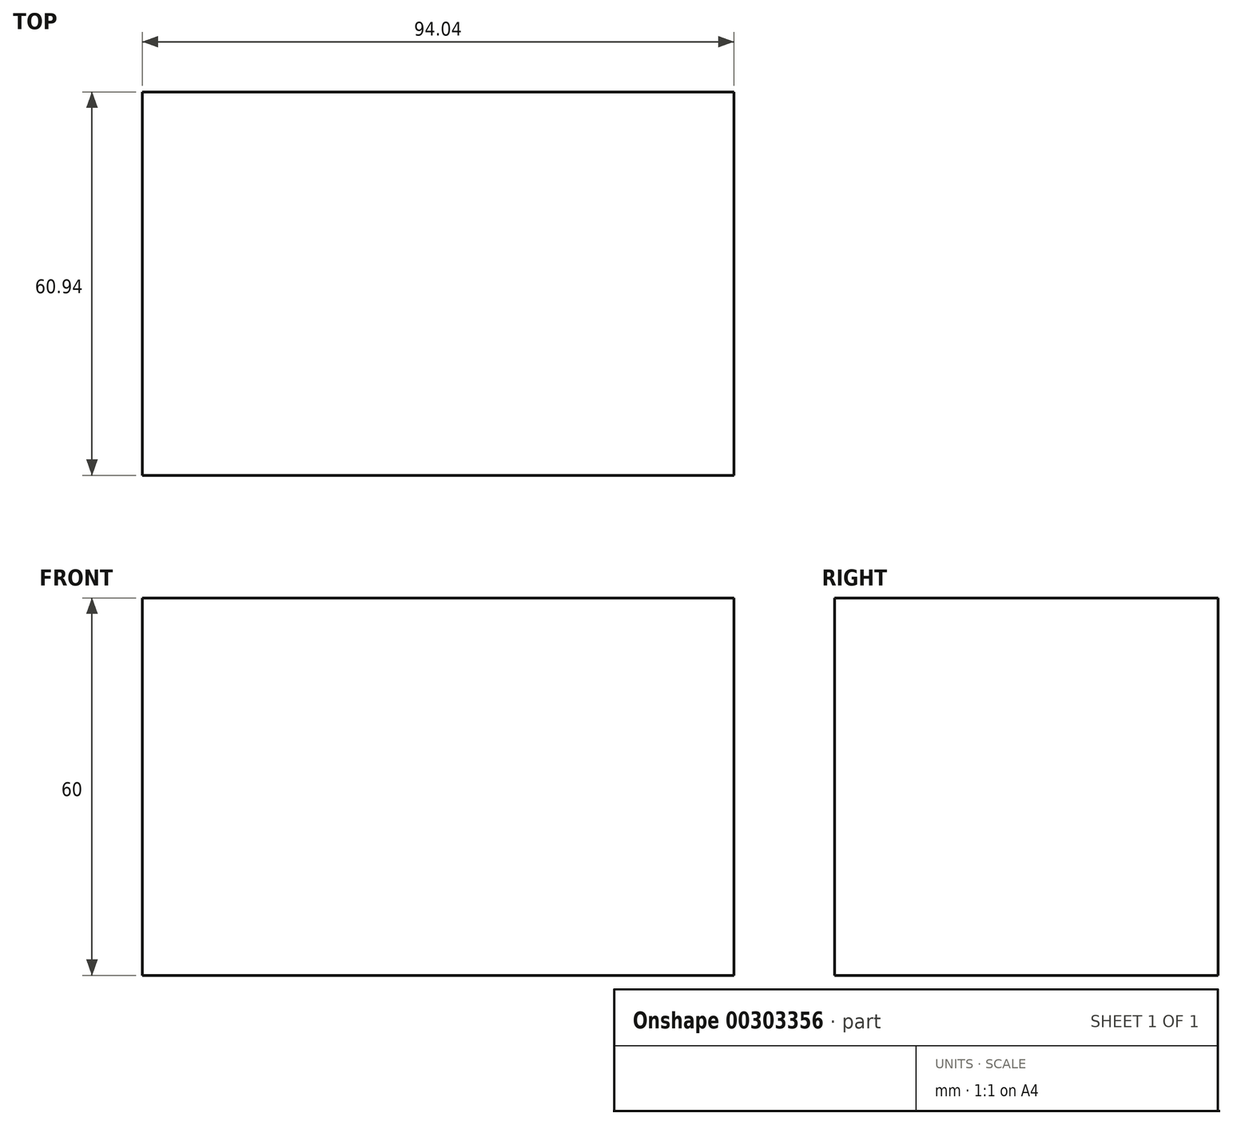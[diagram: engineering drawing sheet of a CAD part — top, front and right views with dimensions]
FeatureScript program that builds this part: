
annotation { "Feature Type Name" : "Feature", "Feature Type Description" : "" }
export const myFeature = defineFeature(function(context is Context, id is Id, definition is map)
    precondition{}
    {
        {
            var Q0;
            Q0=qCreatedBy(makeId("Top.planeOp"),FACE);
            var sketch = newSketch(context, id + "F0", { "sketchPlane" : qUnion([Q0])});
            skLineSegment(sketch, "E0.bottom", {"start": v(-49, -24.97) * mm, "end": v(45.03, -24.97) * mm});
            skLineSegment(sketch, "E0.top", {"start": v(-49, 35.97) * mm, "end": v(45.03, 35.97) * mm});
            skLineSegment(sketch, "E0.left", {"start": v(-49, -24.97) * mm, "end": v(-49, 35.97) * mm});
            skLineSegment(sketch, "E0.right", {"start": v(45.03, -24.97) * mm, "end": v(45.03, 35.97) * mm});
            skSolve(sketch);
        }
        {
            var Q0;
            Q0=makeQuery(id+"F0.imprint","IMPRINT",FACE,{"disambiguationData":[TD([[makeQuery(id+"F0.imprint","IMPRINT",EDGE,{"derivedFrom":sQuery(id+"F0.wireOp",EDGE,"E0.bottom")}),1.0]])]});
            extrude(context, id + "F1", {"entities" : qUnion([Q0]), "depth" : 60 * mm});
        }
    });
